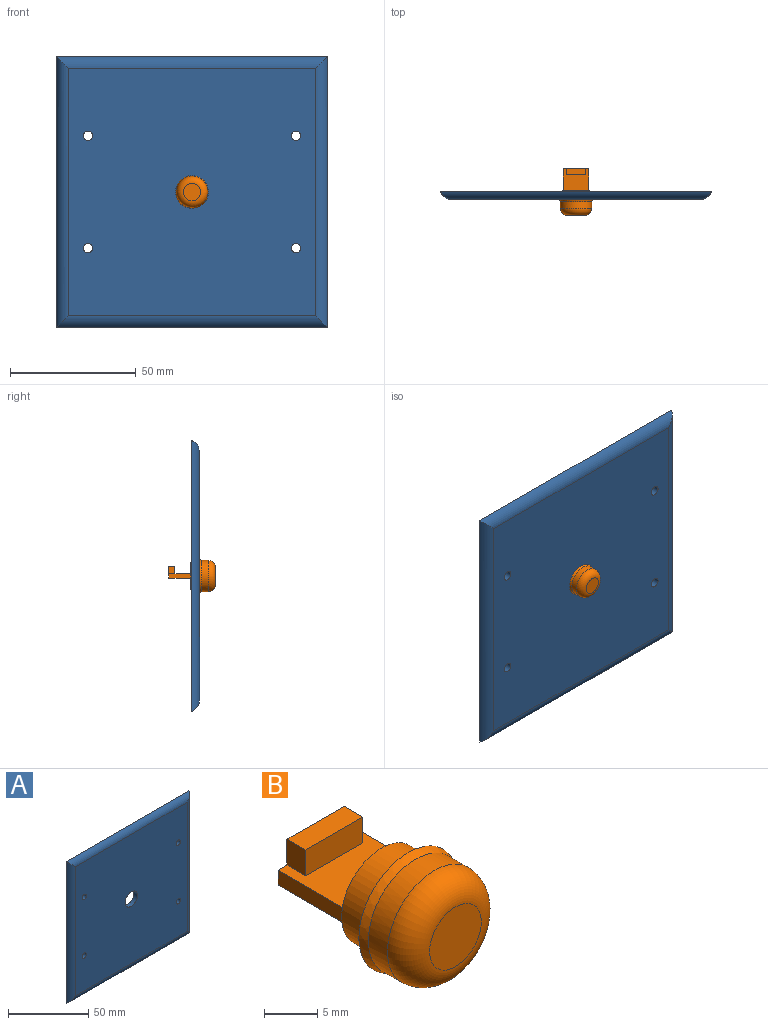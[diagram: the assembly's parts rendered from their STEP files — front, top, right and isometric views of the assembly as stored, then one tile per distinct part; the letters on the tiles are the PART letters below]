
ASSEMBLY  parts=2 mates=1
PART A: 11 faces, bbox 108x3.2x108 mm
  f0: plane 98.53x98.53mm, normal (0,-1,0), area 9567.3mm2, adj f2,f3,f4,f5,f6,f7,f8,f9
  f1: plane 107.95x107.95mm, normal (0,1,0), area 11512mm2, adj f2,f3,f4,f5,f6,f7,f8,f9
  f2: cylinder r=5.08mm len=107.95mm, axis (0,0,-1), area 626.1mm2, adj f0,f1,f3,f4
  f3: cylinder r=5.08mm len=107.95mm, axis (-1,0,0), area 626.1mm2, adj f0,f1,f2,f5
  f4: cylinder r=5.08mm len=107.95mm, axis (-1,0,0), area 626.1mm2, adj f0,f1,f2,f5
  f5: cylinder r=5.08mm len=107.95mm, axis (0,0,-1), area 626.1mm2, adj f0,f1,f3,f4
  f6: cylinder r=1.9mm len=3.8mm, axis (0,1,0), area 37.9mm2, adj f0,f1
  f7: cylinder r=1.9mm len=3.8mm, axis (0,1,0), area 37.9mm2, adj f0,f1
  f8: cylinder r=1.9mm len=3.8mm, axis (0,1,0), area 37.9mm2, adj f0,f1
  f9: cylinder r=1.9mm len=3.8mm, axis (0,1,0), area 37.9mm2, adj f0,f1
  f10: cylinder r=5.52mm len=11.05mm, axis (0,1,0), area 110.2mm2, adj f0,f1
PART B: 16 faces, bbox 13.5x18.6x13.5 mm
  f0: cylinder r=6.22mm len=12.45mm, axis (0,-1,0), area 99.3mm2, adj f5,f6
  f1: plane 13.09x13.09mm, normal (0,1,0), area 47.1mm2, adj f2,f6
  f2: cylinder r=5.27mm len=10.54mm, axis (0,-1,0), area 117.8mm2, adj f1,f3
  f3: plane 10.54x10.54mm, normal (0,1,0), area 70.3mm2, adj f2,f7,f8,f9,f10
  f4: plane 6.86x6.86mm, normal (0,-1,0), area 36.9mm2, adj f5
  f5: torus R=3.43mm, axis (0,-1,0), area 143.6mm2, adj f0,f4
  f6: bspline ~13.08x13.08mm, area 39.9mm2, adj f0,f1
  f7: plane 9.96x8.74mm, normal (0,0,1), area 68.2mm2, adj f3,f8,f10,f11,f12,f13,f14
  f8: plane 8.74x1.7mm, normal (1,0,0), area 14.9mm2, adj f3,f7,f9,f11
  f9: plane 9.96x8.74mm, normal (0,0,-1), area 87mm2, adj f3,f8,f10,f11
  f10: plane 8.74x1.7mm, normal (-1,0,0), area 14.9mm2, adj f3,f7,f9,f11
  f11: plane 9.96x4.67mm, normal (0,1,0), area 39.4mm2, adj f7,f8,f9,f10,f12,f14,f15
  f12: plane 2.97x2.49mm, normal (-1,0,0), area 7.4mm2, adj f7,f11,f13,f15
  f13: plane 7.57x2.97mm, normal (0,-1,0), area 22.5mm2, adj f7,f12,f14,f15
  f14: plane 2.97x2.49mm, normal (1,0,0), area 7.4mm2, adj f7,f11,f13,f15
  f15: plane 7.57x2.49mm, normal (0,0,1), area 18.8mm2, adj f11,f12,f13,f14
PLACE A t=(-58.8,-30.62,2.61)mm
PLACE B t=(-58.8,-40.06,2.61)mm
MATE parallel B.f0 <-> A.f10  axis (0,1,0) through (-58.8,-33.79,2.61)mm
